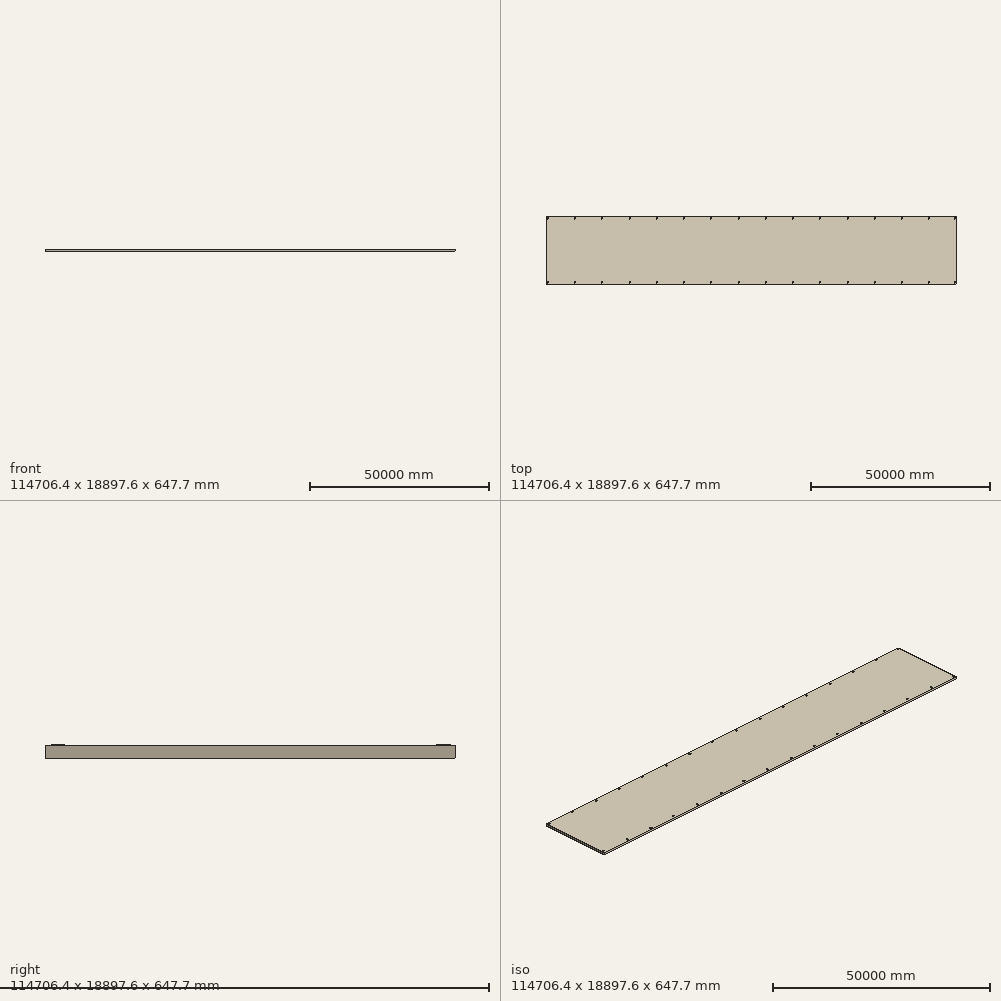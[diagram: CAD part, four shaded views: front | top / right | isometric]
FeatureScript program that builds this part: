
annotation { "Feature Type Name" : "Feature", "Feature Type Description" : "" }
export const myFeature = defineFeature(function(context is Context, id is Id, definition is map)
    precondition{}
    {
        {
            var Q0;
            Q0=qCreatedBy(makeId("Top.planeOp"),FACE);
            var sketch = newSketch(context, id + "F0", { "sketchPlane" : qUnion([Q0])});
            skLineSegment(sketch, "E0.bottom", {"start": v(57353.2, -9448.8) * mm, "end": v(-57353.2, -9448.8) * mm});
            skLineSegment(sketch, "E0.top", {"start": v(57353.2, 9448.8) * mm, "end": v(-57353.2, 9448.8) * mm});
            skLineSegment(sketch, "E0.left", {"start": v(57353.2, -9448.8) * mm, "end": v(57353.2, 9448.8) * mm});
            skLineSegment(sketch, "E0.right", {"start": v(-57353.2, -9448.8) * mm, "end": v(-57353.2, 9448.8) * mm});
            skPoint(sketch, "E0.middle", {"position": v(0, 0) * mm});
            skSolve(sketch);
        }
        {
            var Q0;
            Q0=makeQuery(id+"F0.imprint","IMPRINT",FACE,{"disambiguationData":[TD([[makeQuery(id+"F0.imprint","IMPRINT",EDGE,{"derivedFrom":sQuery(id+"F0.wireOp",EDGE,"E0.bottom")}),-1.0]])]});
            extrude(context, id + "F1", {"entities" : qUnion([Q0]), "depth" : 609.6 * mm});
        }
        {
            var Q0;
            Q0=makeQuery(id+"F1.opExtrude","CAP_FACE",FACE,{"disambiguationData":[OSD([sQuery(id+"F0.wireOp",EDGE,"E0.bottom"),sQuery(id+"F0.wireOp",EDGE,"E0.top"),sQuery(id+"F0.wireOp",EDGE,"E0.left"),sQuery(id+"F0.wireOp",EDGE,"E0.right")])],"isStart":false});
            var sketch = newSketch(context, id + "F2", { "sketchPlane" : qUnion([Q0])});
            skLineSegment(sketch, "E1.bottom", {"start": v(57150, -9194.8) * mm, "end": v(56845.2, -9194.8) * mm});
            skLineSegment(sketch, "E1.top", {"start": v(57150, -8585.2) * mm, "end": v(56845.2, -8585.2) * mm});
            skLineSegment(sketch, "E1.left", {"start": v(57150, -9194.8) * mm, "end": v(57150, -8585.2) * mm});
            skLineSegment(sketch, "E1.right", {"start": v(56845.2, -9194.8) * mm, "end": v(56845.2, -8585.2) * mm});
            skPoint(sketch, "E1.middle", {"position": v(56997.6, -8890) * mm});
            skLineSegment(sketch, "E2", {"start": v(-3997.08, 0) * mm, "end": v(5674.44, 0) * mm});
            skPoint(sketch, "E3.MirrorP", {"position": v(56997.6, 8890) * mm});
            skLineSegment(sketch, "E4.MirrorCS", {"start": v(57150, 9194.8) * mm, "end": v(56845.2, 9194.8) * mm});
            skLineSegment(sketch, "E5.MirrorCS", {"start": v(57150, 8585.2) * mm, "end": v(56845.2, 8585.2) * mm});
            skLineSegment(sketch, "E6.MirrorCS", {"start": v(56845.2, 9194.8) * mm, "end": v(56845.2, 8585.2) * mm});
            skLineSegment(sketch, "E7.MirrorCS", {"start": v(57150, 9194.8) * mm, "end": v(57150, 8585.2) * mm});
            skLineSegment(sketch, "E8.1.0.0", {"start": v(49580.8, 9194.8) * mm, "end": v(49580.8, 8585.2) * mm});
            skLineSegment(sketch, "E8.1.0.1", {"start": v(49885.6, 9194.8) * mm, "end": v(49885.6, 8585.2) * mm});
            skPoint(sketch, "E8.1.0.2", {"position": v(49733.2, 8890) * mm});
            skLineSegment(sketch, "E8.1.0.3", {"start": v(49885.6, 9194.8) * mm, "end": v(49580.8, 9194.8) * mm});
            skLineSegment(sketch, "E8.1.0.4", {"start": v(49885.6, 8585.2) * mm, "end": v(49580.8, 8585.2) * mm});
            skLineSegment(sketch, "E8.1.0.5", {"start": v(49885.6, -9194.8) * mm, "end": v(49580.8, -9194.8) * mm});
            skLineSegment(sketch, "E8.1.0.6", {"start": v(49885.6, -8585.2) * mm, "end": v(49580.8, -8585.2) * mm});
            skPoint(sketch, "E8.1.0.7", {"position": v(49733.2, -8890) * mm});
            skLineSegment(sketch, "E8.1.0.8", {"start": v(49885.6, -9194.8) * mm, "end": v(49885.6, -8585.2) * mm});
            skLineSegment(sketch, "E8.1.0.9", {"start": v(49580.8, -9194.8) * mm, "end": v(49580.8, -8585.2) * mm});
            skLineSegment(sketch, "E8.direction1", {"start": v(56845.2, 8585.2) * mm, "end": v(49580.8, 8585.2) * mm, "construction": true});
            skPoint(sketch, "E9.1.0.0", {"position": v(42113.2, -8890) * mm});
            skPoint(sketch, "E9.1.0.1", {"position": v(42113.2, 8890) * mm});
            skLineSegment(sketch, "E9.1.0.2", {"start": v(41960.8, -9194.8) * mm, "end": v(41960.8, -8585.2) * mm});
            skLineSegment(sketch, "E9.1.0.3", {"start": v(42265.6, 9194.8) * mm, "end": v(41960.8, 9194.8) * mm});
            skLineSegment(sketch, "E9.1.0.4", {"start": v(42265.6, 9194.8) * mm, "end": v(42265.6, 8585.2) * mm});
            skLineSegment(sketch, "E9.1.0.5", {"start": v(41960.8, 9194.8) * mm, "end": v(41960.8, 8585.2) * mm});
            skLineSegment(sketch, "E9.1.0.6", {"start": v(42265.6, -9194.8) * mm, "end": v(41960.8, -9194.8) * mm});
            skLineSegment(sketch, "E9.1.0.7", {"start": v(42265.6, -8585.2) * mm, "end": v(41960.8, -8585.2) * mm});
            skLineSegment(sketch, "E9.1.0.8", {"start": v(42265.6, -9194.8) * mm, "end": v(42265.6, -8585.2) * mm});
            skLineSegment(sketch, "E9.1.0.9", {"start": v(42265.6, 8585.2) * mm, "end": v(41960.8, 8585.2) * mm});
            skPoint(sketch, "E9.2.0.0", {"position": v(34493.2, -8890) * mm});
            skPoint(sketch, "E9.2.0.1", {"position": v(34493.2, 8890) * mm});
            skLineSegment(sketch, "E9.2.0.2", {"start": v(34340.8, -9194.8) * mm, "end": v(34340.8, -8585.2) * mm});
            skLineSegment(sketch, "E9.2.0.3", {"start": v(34645.6, 9194.8) * mm, "end": v(34340.8, 9194.8) * mm});
            skLineSegment(sketch, "E9.2.0.4", {"start": v(34645.6, 9194.8) * mm, "end": v(34645.6, 8585.2) * mm});
            skLineSegment(sketch, "E9.2.0.5", {"start": v(34340.8, 9194.8) * mm, "end": v(34340.8, 8585.2) * mm});
            skLineSegment(sketch, "E9.2.0.6", {"start": v(34645.6, -9194.8) * mm, "end": v(34340.8, -9194.8) * mm});
            skLineSegment(sketch, "E9.2.0.7", {"start": v(34645.6, -8585.2) * mm, "end": v(34340.8, -8585.2) * mm});
            skLineSegment(sketch, "E9.2.0.8", {"start": v(34645.6, -9194.8) * mm, "end": v(34645.6, -8585.2) * mm});
            skLineSegment(sketch, "E9.2.0.9", {"start": v(34645.6, 8585.2) * mm, "end": v(34340.8, 8585.2) * mm});
            skPoint(sketch, "E9.3.0.0", {"position": v(26873.2, -8890) * mm});
            skPoint(sketch, "E9.3.0.1", {"position": v(26873.2, 8890) * mm});
            skLineSegment(sketch, "E9.3.0.2", {"start": v(26720.8, -9194.8) * mm, "end": v(26720.8, -8585.2) * mm});
            skLineSegment(sketch, "E9.3.0.3", {"start": v(27025.6, 9194.8) * mm, "end": v(26720.8, 9194.8) * mm});
            skLineSegment(sketch, "E9.3.0.4", {"start": v(27025.6, 9194.8) * mm, "end": v(27025.6, 8585.2) * mm});
            skLineSegment(sketch, "E9.3.0.5", {"start": v(26720.8, 9194.8) * mm, "end": v(26720.8, 8585.2) * mm});
            skLineSegment(sketch, "E9.3.0.6", {"start": v(27025.6, -9194.8) * mm, "end": v(26720.8, -9194.8) * mm});
            skLineSegment(sketch, "E9.3.0.7", {"start": v(27025.6, -8585.2) * mm, "end": v(26720.8, -8585.2) * mm});
            skLineSegment(sketch, "E9.3.0.8", {"start": v(27025.6, -9194.8) * mm, "end": v(27025.6, -8585.2) * mm});
            skLineSegment(sketch, "E9.3.0.9", {"start": v(27025.6, 8585.2) * mm, "end": v(26720.8, 8585.2) * mm});
            skPoint(sketch, "E9.4.0.0", {"position": v(19253.2, -8890) * mm});
            skPoint(sketch, "E9.4.0.1", {"position": v(19253.2, 8890) * mm});
            skLineSegment(sketch, "E9.4.0.2", {"start": v(19100.8, -9194.8) * mm, "end": v(19100.8, -8585.2) * mm});
            skLineSegment(sketch, "E9.4.0.3", {"start": v(19405.6, 9194.8) * mm, "end": v(19100.8, 9194.8) * mm});
            skLineSegment(sketch, "E9.4.0.4", {"start": v(19405.6, 9194.8) * mm, "end": v(19405.6, 8585.2) * mm});
            skLineSegment(sketch, "E9.4.0.5", {"start": v(19100.8, 9194.8) * mm, "end": v(19100.8, 8585.2) * mm});
            skLineSegment(sketch, "E9.4.0.6", {"start": v(19405.6, -9194.8) * mm, "end": v(19100.8, -9194.8) * mm});
            skLineSegment(sketch, "E9.4.0.7", {"start": v(19405.6, -8585.2) * mm, "end": v(19100.8, -8585.2) * mm});
            skLineSegment(sketch, "E9.4.0.8", {"start": v(19405.6, -9194.8) * mm, "end": v(19405.6, -8585.2) * mm});
            skLineSegment(sketch, "E9.4.0.9", {"start": v(19405.6, 8585.2) * mm, "end": v(19100.8, 8585.2) * mm});
            skPoint(sketch, "E9.5.0.0", {"position": v(11633.2, -8890) * mm});
            skPoint(sketch, "E9.5.0.1", {"position": v(11633.2, 8890) * mm});
            skLineSegment(sketch, "E9.5.0.2", {"start": v(11480.8, -9194.8) * mm, "end": v(11480.8, -8585.2) * mm});
            skLineSegment(sketch, "E9.5.0.3", {"start": v(11785.6, 9194.8) * mm, "end": v(11480.8, 9194.8) * mm});
            skLineSegment(sketch, "E9.5.0.4", {"start": v(11785.6, 9194.8) * mm, "end": v(11785.6, 8585.2) * mm});
            skLineSegment(sketch, "E9.5.0.5", {"start": v(11480.8, 9194.8) * mm, "end": v(11480.8, 8585.2) * mm});
            skLineSegment(sketch, "E9.5.0.6", {"start": v(11785.6, -9194.8) * mm, "end": v(11480.8, -9194.8) * mm});
            skLineSegment(sketch, "E9.5.0.7", {"start": v(11785.6, -8585.2) * mm, "end": v(11480.8, -8585.2) * mm});
            skLineSegment(sketch, "E9.5.0.8", {"start": v(11785.6, -9194.8) * mm, "end": v(11785.6, -8585.2) * mm});
            skLineSegment(sketch, "E9.5.0.9", {"start": v(11785.6, 8585.2) * mm, "end": v(11480.8, 8585.2) * mm});
            skPoint(sketch, "E9.6.0.0", {"position": v(4013.2, -8890) * mm});
            skPoint(sketch, "E9.6.0.1", {"position": v(4013.2, 8890) * mm});
            skLineSegment(sketch, "E9.6.0.2", {"start": v(3860.8, -9194.8) * mm, "end": v(3860.8, -8585.2) * mm});
            skLineSegment(sketch, "E9.6.0.3", {"start": v(4165.6, 9194.8) * mm, "end": v(3860.8, 9194.8) * mm});
            skLineSegment(sketch, "E9.6.0.4", {"start": v(4165.6, 9194.8) * mm, "end": v(4165.6, 8585.2) * mm});
            skLineSegment(sketch, "E9.6.0.5", {"start": v(3860.8, 9194.8) * mm, "end": v(3860.8, 8585.2) * mm});
            skLineSegment(sketch, "E9.6.0.6", {"start": v(4165.6, -9194.8) * mm, "end": v(3860.8, -9194.8) * mm});
            skLineSegment(sketch, "E9.6.0.7", {"start": v(4165.6, -8585.2) * mm, "end": v(3860.8, -8585.2) * mm});
            skLineSegment(sketch, "E9.6.0.8", {"start": v(4165.6, -9194.8) * mm, "end": v(4165.6, -8585.2) * mm});
            skLineSegment(sketch, "E9.6.0.9", {"start": v(4165.6, 8585.2) * mm, "end": v(3860.8, 8585.2) * mm});
            skPoint(sketch, "E9.7.0.0", {"position": v(-3606.8, -8890) * mm});
            skPoint(sketch, "E9.7.0.1", {"position": v(-3606.8, 8890) * mm});
            skLineSegment(sketch, "E9.7.0.2", {"start": v(-3759.2, -9194.8) * mm, "end": v(-3759.2, -8585.2) * mm});
            skLineSegment(sketch, "E9.7.0.3", {"start": v(-3454.4, 9194.8) * mm, "end": v(-3759.2, 9194.8) * mm});
            skLineSegment(sketch, "E9.7.0.4", {"start": v(-3454.4, 9194.8) * mm, "end": v(-3454.4, 8585.2) * mm});
            skLineSegment(sketch, "E9.7.0.5", {"start": v(-3759.2, 9194.8) * mm, "end": v(-3759.2, 8585.2) * mm});
            skLineSegment(sketch, "E9.7.0.6", {"start": v(-3454.4, -9194.8) * mm, "end": v(-3759.2, -9194.8) * mm});
            skLineSegment(sketch, "E9.7.0.7", {"start": v(-3454.4, -8585.2) * mm, "end": v(-3759.2, -8585.2) * mm});
            skLineSegment(sketch, "E9.7.0.8", {"start": v(-3454.4, -9194.8) * mm, "end": v(-3454.4, -8585.2) * mm});
            skLineSegment(sketch, "E9.7.0.9", {"start": v(-3454.4, 8585.2) * mm, "end": v(-3759.2, 8585.2) * mm});
            skPoint(sketch, "E9.8.0.0", {"position": v(-11226.8, -8890) * mm});
            skPoint(sketch, "E9.8.0.1", {"position": v(-11226.8, 8890) * mm});
            skLineSegment(sketch, "E9.8.0.2", {"start": v(-11379.2, -9194.8) * mm, "end": v(-11379.2, -8585.2) * mm});
            skLineSegment(sketch, "E9.8.0.3", {"start": v(-11074.4, 9194.8) * mm, "end": v(-11379.2, 9194.8) * mm});
            skLineSegment(sketch, "E9.8.0.4", {"start": v(-11074.4, 9194.8) * mm, "end": v(-11074.4, 8585.2) * mm});
            skLineSegment(sketch, "E9.8.0.5", {"start": v(-11379.2, 9194.8) * mm, "end": v(-11379.2, 8585.2) * mm});
            skLineSegment(sketch, "E9.8.0.6", {"start": v(-11074.4, -9194.8) * mm, "end": v(-11379.2, -9194.8) * mm});
            skLineSegment(sketch, "E9.8.0.7", {"start": v(-11074.4, -8585.2) * mm, "end": v(-11379.2, -8585.2) * mm});
            skLineSegment(sketch, "E9.8.0.8", {"start": v(-11074.4, -9194.8) * mm, "end": v(-11074.4, -8585.2) * mm});
            skLineSegment(sketch, "E9.8.0.9", {"start": v(-11074.4, 8585.2) * mm, "end": v(-11379.2, 8585.2) * mm});
            skPoint(sketch, "E9.9.0.0", {"position": v(-18846.8, -8890) * mm});
            skPoint(sketch, "E9.9.0.1", {"position": v(-18846.8, 8890) * mm});
            skLineSegment(sketch, "E9.9.0.2", {"start": v(-18999.2, -9194.8) * mm, "end": v(-18999.2, -8585.2) * mm});
            skLineSegment(sketch, "E9.9.0.3", {"start": v(-18694.4, 9194.8) * mm, "end": v(-18999.2, 9194.8) * mm});
            skLineSegment(sketch, "E9.9.0.4", {"start": v(-18694.4, 9194.8) * mm, "end": v(-18694.4, 8585.2) * mm});
            skLineSegment(sketch, "E9.9.0.5", {"start": v(-18999.2, 9194.8) * mm, "end": v(-18999.2, 8585.2) * mm});
            skLineSegment(sketch, "E9.9.0.6", {"start": v(-18694.4, -9194.8) * mm, "end": v(-18999.2, -9194.8) * mm});
            skLineSegment(sketch, "E9.9.0.7", {"start": v(-18694.4, -8585.2) * mm, "end": v(-18999.2, -8585.2) * mm});
            skLineSegment(sketch, "E9.9.0.8", {"start": v(-18694.4, -9194.8) * mm, "end": v(-18694.4, -8585.2) * mm});
            skLineSegment(sketch, "E9.9.0.9", {"start": v(-18694.4, 8585.2) * mm, "end": v(-18999.2, 8585.2) * mm});
            skPoint(sketch, "E9.10.0.0", {"position": v(-26466.8, -8890) * mm});
            skPoint(sketch, "E9.10.0.1", {"position": v(-26466.8, 8890) * mm});
            skLineSegment(sketch, "E9.10.0.2", {"start": v(-26619.2, -9194.8) * mm, "end": v(-26619.2, -8585.2) * mm});
            skLineSegment(sketch, "E9.10.0.3", {"start": v(-26314.4, 9194.8) * mm, "end": v(-26619.2, 9194.8) * mm});
            skLineSegment(sketch, "E9.10.0.4", {"start": v(-26314.4, 9194.8) * mm, "end": v(-26314.4, 8585.2) * mm});
            skLineSegment(sketch, "E9.10.0.5", {"start": v(-26619.2, 9194.8) * mm, "end": v(-26619.2, 8585.2) * mm});
            skLineSegment(sketch, "E9.10.0.6", {"start": v(-26314.4, -9194.8) * mm, "end": v(-26619.2, -9194.8) * mm});
            skLineSegment(sketch, "E9.10.0.7", {"start": v(-26314.4, -8585.2) * mm, "end": v(-26619.2, -8585.2) * mm});
            skLineSegment(sketch, "E9.10.0.8", {"start": v(-26314.4, -9194.8) * mm, "end": v(-26314.4, -8585.2) * mm});
            skLineSegment(sketch, "E9.10.0.9", {"start": v(-26314.4, 8585.2) * mm, "end": v(-26619.2, 8585.2) * mm});
            skPoint(sketch, "E9.11.0.0", {"position": v(-34086.8, -8890) * mm});
            skPoint(sketch, "E9.11.0.1", {"position": v(-34086.8, 8890) * mm});
            skLineSegment(sketch, "E9.11.0.2", {"start": v(-34239.2, -9194.8) * mm, "end": v(-34239.2, -8585.2) * mm});
            skLineSegment(sketch, "E9.11.0.3", {"start": v(-33934.4, 9194.8) * mm, "end": v(-34239.2, 9194.8) * mm});
            skLineSegment(sketch, "E9.11.0.4", {"start": v(-33934.4, 9194.8) * mm, "end": v(-33934.4, 8585.2) * mm});
            skLineSegment(sketch, "E9.11.0.5", {"start": v(-34239.2, 9194.8) * mm, "end": v(-34239.2, 8585.2) * mm});
            skLineSegment(sketch, "E9.11.0.6", {"start": v(-33934.4, -9194.8) * mm, "end": v(-34239.2, -9194.8) * mm});
            skLineSegment(sketch, "E9.11.0.7", {"start": v(-33934.4, -8585.2) * mm, "end": v(-34239.2, -8585.2) * mm});
            skLineSegment(sketch, "E9.11.0.8", {"start": v(-33934.4, -9194.8) * mm, "end": v(-33934.4, -8585.2) * mm});
            skLineSegment(sketch, "E9.11.0.9", {"start": v(-33934.4, 8585.2) * mm, "end": v(-34239.2, 8585.2) * mm});
            skPoint(sketch, "E9.12.0.0", {"position": v(-41706.8, -8890) * mm});
            skPoint(sketch, "E9.12.0.1", {"position": v(-41706.8, 8890) * mm});
            skLineSegment(sketch, "E9.12.0.2", {"start": v(-41859.2, -9194.8) * mm, "end": v(-41859.2, -8585.2) * mm});
            skLineSegment(sketch, "E9.12.0.3", {"start": v(-41554.4, 9194.8) * mm, "end": v(-41859.2, 9194.8) * mm});
            skLineSegment(sketch, "E9.12.0.4", {"start": v(-41554.4, 9194.8) * mm, "end": v(-41554.4, 8585.2) * mm});
            skLineSegment(sketch, "E9.12.0.5", {"start": v(-41859.2, 9194.8) * mm, "end": v(-41859.2, 8585.2) * mm});
            skLineSegment(sketch, "E9.12.0.6", {"start": v(-41554.4, -9194.8) * mm, "end": v(-41859.2, -9194.8) * mm});
            skLineSegment(sketch, "E9.12.0.7", {"start": v(-41554.4, -8585.2) * mm, "end": v(-41859.2, -8585.2) * mm});
            skLineSegment(sketch, "E9.12.0.8", {"start": v(-41554.4, -9194.8) * mm, "end": v(-41554.4, -8585.2) * mm});
            skLineSegment(sketch, "E9.12.0.9", {"start": v(-41554.4, 8585.2) * mm, "end": v(-41859.2, 8585.2) * mm});
            skPoint(sketch, "E9.13.0.0", {"position": v(-49326.8, -8890) * mm});
            skPoint(sketch, "E9.13.0.1", {"position": v(-49326.8, 8890) * mm});
            skLineSegment(sketch, "E9.13.0.2", {"start": v(-49479.2, -9194.8) * mm, "end": v(-49479.2, -8585.2) * mm});
            skLineSegment(sketch, "E9.13.0.3", {"start": v(-49174.4, 9194.8) * mm, "end": v(-49479.2, 9194.8) * mm});
            skLineSegment(sketch, "E9.13.0.4", {"start": v(-49174.4, 9194.8) * mm, "end": v(-49174.4, 8585.2) * mm});
            skLineSegment(sketch, "E9.13.0.5", {"start": v(-49479.2, 9194.8) * mm, "end": v(-49479.2, 8585.2) * mm});
            skLineSegment(sketch, "E9.13.0.6", {"start": v(-49174.4, -9194.8) * mm, "end": v(-49479.2, -9194.8) * mm});
            skLineSegment(sketch, "E9.13.0.7", {"start": v(-49174.4, -8585.2) * mm, "end": v(-49479.2, -8585.2) * mm});
            skLineSegment(sketch, "E9.13.0.8", {"start": v(-49174.4, -9194.8) * mm, "end": v(-49174.4, -8585.2) * mm});
            skLineSegment(sketch, "E9.13.0.9", {"start": v(-49174.4, 8585.2) * mm, "end": v(-49479.2, 8585.2) * mm});
            skLineSegment(sketch, "E9.direction1", {"start": v(49580.8, -9194.8) * mm, "end": v(41960.8, -9194.8) * mm, "construction": true});
            skLineSegment(sketch, "E10", {"start": v(0, 2317.78) * mm, "end": v(0, -2438.18) * mm});
            skPoint(sketch, "E11.MirrorP", {"position": v(-56997.6, -8890) * mm});
            skPoint(sketch, "E12.MirrorP", {"position": v(-56997.6, 8890) * mm});
            skPoint(sketch, "E13.MirrorCS.end.orphan", {"position": v(-57150, -8585.2) * mm});
            skPoint(sketch, "E14.MirrorCS.end.orphan", {"position": v(-56845.2, -8585.2) * mm});
            skPoint(sketch, "E15.MirrorCS.end.orphan", {"position": v(-56845.2, -9194.8) * mm});
            skPoint(sketch, "E15.MirrorCS.start.orphan", {"position": v(-57150, -9194.8) * mm});
            skPoint(sketch, "E16.MirrorCS.start.orphan", {"position": v(-57150, 9194.8) * mm});
            skPoint(sketch, "E17.MirrorCS.start.orphan", {"position": v(-56845.2, 9194.8) * mm});
            skPoint(sketch, "E18.MirrorCS.end.orphan", {"position": v(-56845.2, 8585.2) * mm});
            skPoint(sketch, "E18.MirrorCS.start.orphan", {"position": v(-57150, 8585.2) * mm});
            skLineSegment(sketch, "E19.0.1.0", {"start": v(-49479.2, -9169.4) * mm, "end": v(-49479.2, -8559.8) * mm});
            skLineSegment(sketch, "E19.0.1.1", {"start": v(-49174.4, -9169.4) * mm, "end": v(-49174.4, -8559.8) * mm});
            skLineSegment(sketch, "E19.0.1.2", {"start": v(-49174.4, -8559.8) * mm, "end": v(-49479.2, -8559.8) * mm});
            skLineSegment(sketch, "E19.0.1.3", {"start": v(-49174.4, -9169.4) * mm, "end": v(-49479.2, -9169.4) * mm});
            skPoint(sketch, "E19.0.1.4", {"position": v(-49326.8, -8864.6) * mm});
            skLineSegment(sketch, "E19.0.1.5", {"start": v(-49174.4, 9220.2) * mm, "end": v(-49479.2, 9220.2) * mm});
            skLineSegment(sketch, "E19.0.1.6", {"start": v(-49479.2, 9220.2) * mm, "end": v(-49479.2, 8610.6) * mm});
            skLineSegment(sketch, "E19.0.1.7", {"start": v(-49174.4, 8610.6) * mm, "end": v(-49479.2, 8610.6) * mm});
            skLineSegment(sketch, "E19.0.1.8", {"start": v(-49174.4, 9220.2) * mm, "end": v(-49174.4, 8610.6) * mm});
            skLineSegment(sketch, "E19.1.0.0", {"start": v(-57099.2, -9194.8) * mm, "end": v(-57099.2, -8585.2) * mm});
            skLineSegment(sketch, "E19.1.0.1", {"start": v(-56794.4, -9194.8) * mm, "end": v(-56794.4, -8585.2) * mm});
            skLineSegment(sketch, "E19.1.0.2", {"start": v(-56794.4, -8585.2) * mm, "end": v(-57099.2, -8585.2) * mm});
            skLineSegment(sketch, "E19.1.0.3", {"start": v(-56794.4, -9194.8) * mm, "end": v(-57099.2, -9194.8) * mm});
            skPoint(sketch, "E19.1.0.4", {"position": v(-56946.8, -8890) * mm});
            skLineSegment(sketch, "E19.1.0.5", {"start": v(-56794.4, 9194.8) * mm, "end": v(-57099.2, 9194.8) * mm});
            skLineSegment(sketch, "E19.1.0.6", {"start": v(-57099.2, 9194.8) * mm, "end": v(-57099.2, 8585.2) * mm});
            skLineSegment(sketch, "E19.1.0.7", {"start": v(-56794.4, 8585.2) * mm, "end": v(-57099.2, 8585.2) * mm});
            skLineSegment(sketch, "E19.1.0.8", {"start": v(-56794.4, 9194.8) * mm, "end": v(-56794.4, 8585.2) * mm});
            skLineSegment(sketch, "E19.1.1.0", {"start": v(-57099.2, -9169.4) * mm, "end": v(-57099.2, -8559.8) * mm});
            skLineSegment(sketch, "E19.1.1.1", {"start": v(-56794.4, -9169.4) * mm, "end": v(-56794.4, -8559.8) * mm});
            skLineSegment(sketch, "E19.1.1.2", {"start": v(-56794.4, -8559.8) * mm, "end": v(-57099.2, -8559.8) * mm});
            skLineSegment(sketch, "E19.1.1.3", {"start": v(-56794.4, -9169.4) * mm, "end": v(-57099.2, -9169.4) * mm});
            skPoint(sketch, "E19.1.1.4", {"position": v(-56946.8, -8864.6) * mm});
            skLineSegment(sketch, "E19.1.1.5", {"start": v(-56794.4, 9220.2) * mm, "end": v(-57099.2, 9220.2) * mm});
            skLineSegment(sketch, "E19.1.1.6", {"start": v(-57099.2, 9220.2) * mm, "end": v(-57099.2, 8610.6) * mm});
            skLineSegment(sketch, "E19.1.1.7", {"start": v(-56794.4, 8610.6) * mm, "end": v(-57099.2, 8610.6) * mm});
            skLineSegment(sketch, "E19.1.1.8", {"start": v(-56794.4, 9220.2) * mm, "end": v(-56794.4, 8610.6) * mm});
            skLineSegment(sketch, "E19.direction1", {"start": v(-49479.2, -9194.8) * mm, "end": v(-57099.2, -9194.8) * mm, "construction": true});
            skLineSegment(sketch, "E19.direction2", {"start": v(-49479.2, -9194.8) * mm, "end": v(-49479.2, -9169.4) * mm, "construction": true});
            skSolve(sketch);
        }
        {
            var Q0;
            Q0 = qSketchRegion(id + "F2", true);
            extrude(context, id + "F3", {"entities" : qUnion([Q0]), "operationType" : NewBodyOperationType.ADD, "depth" : 38.1 * mm});
        }
    });
